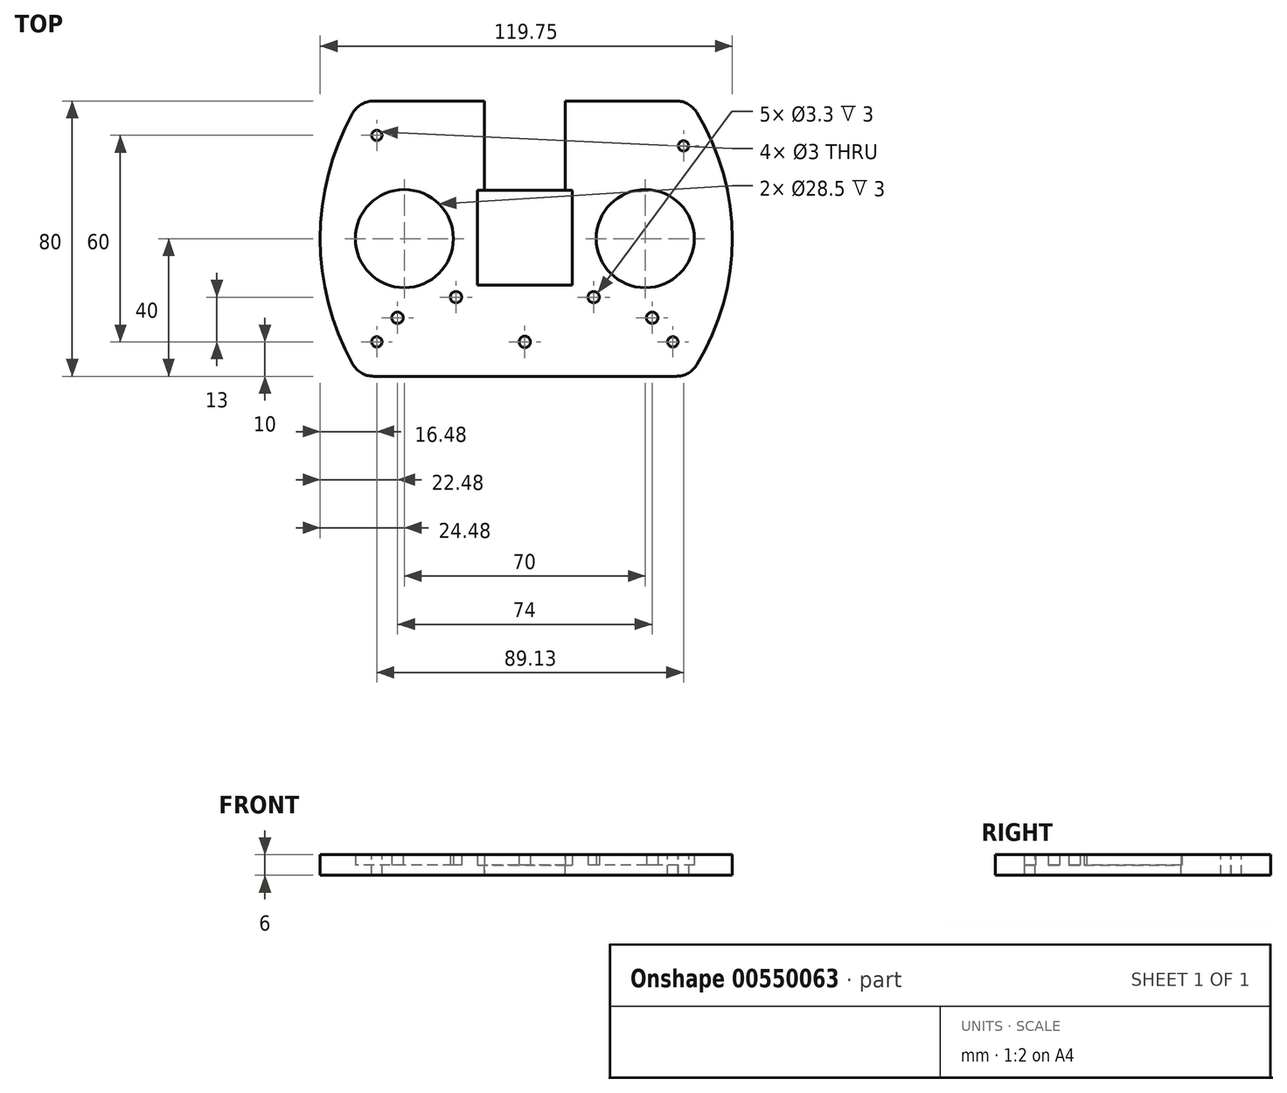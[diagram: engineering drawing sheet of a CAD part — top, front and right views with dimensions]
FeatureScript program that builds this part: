
annotation { "Feature Type Name" : "Feature", "Feature Type Description" : "" }
export const myFeature = defineFeature(function(context is Context, id is Id, definition is map)
    precondition{}
    {
        {
            var Q0;
            Q0=qCreatedBy(makeId("Top.planeOp"),FACE);
            var sketch = newSketch(context, id + "F0", { "sketchPlane" : qUnion([Q0])});
            skLineSegment(sketch, "E0.bottom", {"start": v(-45.1, 35) * mm, "end": v(45.1, 35) * mm});
            skLineSegment(sketch, "E0.top", {"start": v(-45.1, -35) * mm, "end": v(45.1, -35) * mm});
            skArc(sketch, "E1", {"start": v(-45.1, 35) * mm, "mid": v(-54.48, 0) * mm, "end": v(-45.1, -35) * mm});
            skArc(sketch, "E2", {"start": v(45.1, -35) * mm, "mid": v(55.27, 0) * mm, "end": v(45.1, 35) * mm});
            skCircle(sketch, "E3", {"center": v(-43, 30) * mm, "radius": 1.5 * mm});
            skCircle(sketch, "E4", {"center": v(-43, -30) * mm, "radius": 1.5 * mm});
            skLineSegment(sketch, "E5", {"start": v(-43, 30) * mm, "end": v(-43, -30) * mm, "construction": true});
            skCircle(sketch, "E6.MirrorC", {"center": v(43, -30) * mm, "radius": 1.5 * mm});
            skCircle(sketch, "E7.MirrorC", {"center": v(46.13, 26.95) * mm, "radius": 1.5 * mm});
            skSolve(sketch);
        }
        {
            var Q0;
            Q0=makeQuery(id+"F0.imprint","IMPRINT",FACE,{"disambiguationData":[TD([[makeQuery(id+"F0.imprint","IMPRINT",EDGE,{"derivedFrom":sQuery(id+"F0.wireOp",EDGE,"E0.bottom")}),-1.0]])]});
            extrude(context, id + "F1", {"entities" : qUnion([Q0]), "oppositeDirection" : true, "depth" : 3 * mm, "offsetDistance" : 25 * mm});
        }
        {
            var Q0;
            Q0 = qSketchRegion(id + "F0", true);
            extrude(context, id + "F2", {"entities" : qUnion([Q0]), "depth" : 3 * mm, "offsetDistance" : 25 * mm});
        }
        {
            var Q0;
            Q0=qCreatedBy(makeId("Top.planeOp"),FACE);
            var sketch = newSketch(context, id + "F3", { "sketchPlane" : qUnion([Q0])});
            skLineSegment(sketch, "E8.bottom", {"start": v(-13.75, 14) * mm, "end": v(-11.75, 14) * mm});
            skLineSegment(sketch, "E8.top", {"start": v(-13.75, -13.5) * mm, "end": v(13.75, -13.5) * mm});
            skLineSegment(sketch, "E8.left", {"start": v(-13.75, 14) * mm, "end": v(-13.75, -13.5) * mm});
            skLineSegment(sketch, "E8.right", {"start": v(13.75, 14) * mm, "end": v(13.75, -13.5) * mm});
            skCircle(sketch, "E9", {"center": v(-35, 0) * mm, "radius": 14.25 * mm});
            skCircle(sketch, "E10.MirrorC", {"center": v(35, 0) * mm, "radius": 14.25 * mm});
            skCircle(sketch, "E11", {"center": v(-37, -23) * mm, "radius": 1.65 * mm});
            skCircle(sketch, "E12", {"center": v(-20, -17) * mm, "radius": 1.65 * mm});
            skCircle(sketch, "E13", {"center": v(0, -30) * mm, "radius": 1.65 * mm});
            skCircle(sketch, "E14.MirrorC", {"center": v(37, -23) * mm, "radius": 1.65 * mm});
            skCircle(sketch, "E15.MirrorC", {"center": v(20, -17) * mm, "radius": 1.65 * mm});
            skLineSegment(sketch, "E16", {"start": v(-11.75, 14) * mm, "end": v(-11.75, 43.57) * mm});
            skLineSegment(sketch, "E17", {"start": v(-11.75, 43.57) * mm, "end": v(11.75, 43.57) * mm});
            skLineSegment(sketch, "E18", {"start": v(11.75, 43.57) * mm, "end": v(11.75, 14) * mm});
            skLineSegment(sketch, "E19.trimOffspring", {"start": v(11.75, 14) * mm, "end": v(13.75, 14) * mm});
            skSolve(sketch);
        }
        {
            var Q0;
            Q0 = qSketchRegion(id + "F3", true);
            extrude(context, id + "F4", {"entities" : qUnion([Q0]), "operationType" : NewBodyOperationType.REMOVE, "depth" : 25 * mm, "offsetDistance" : 25 * mm});
        }
        {
            var Q0;
            Q0=qCreatedBy(makeId("Top.planeOp"),FACE);
            var sketch = newSketch(context, id + "F5", { "sketchPlane" : qUnion([Q0])});
            skArc(sketch, "E20.0", {"start": v(-50.05, -36.4) * mm, "mid": v(-59.48, 0) * mm, "end": v(-50.05, 36.4) * mm});
            skLineSegment(sketch, "E20.1", {"start": v(43.99, -40) * mm, "end": v(-43.93, -40) * mm});
            skArc(sketch, "E20.2", {"start": v(49.96, 36.65) * mm, "mid": v(60.27, 0) * mm, "end": v(49.96, -36.65) * mm});
            skLineSegment(sketch, "E20.3", {"start": v(-43.93, 40) * mm, "end": v(43.99, 40) * mm});
            skArc(sketch, "E21.0", {"start": v(-44.52, -34) * mm, "mid": v(-53.48, 0) * mm, "end": v(-44.52, 34) * mm});
            skLineSegment(sketch, "E21.1", {"start": v(44.55, -34) * mm, "end": v(-44.52, -34) * mm});
            skArc(sketch, "E21.2", {"start": v(44.55, 34) * mm, "mid": v(54.27, 0) * mm, "end": v(44.55, -34) * mm});
            skLineSegment(sketch, "E21.3", {"start": v(-44.52, 34) * mm, "end": v(44.55, 34) * mm});
            skPoint(sketch, "E22.visualSharp", {"position": v(47.78, 40) * mm});
            skArc(sketch, "E22.filletArc", {"start": v(49.96, 36.65) * mm, "mid": v(47.41, 39.1) * mm, "end": v(43.99, 40) * mm});
            skPoint(sketch, "E23.visualSharp", {"position": v(47.78, -40) * mm});
            skArc(sketch, "E23.filletArc", {"start": v(43.99, -40) * mm, "mid": v(47.41, -39.1) * mm, "end": v(49.96, -36.65) * mm});
            skPoint(sketch, "E24.visualSharp", {"position": v(-47.92, -40) * mm});
            skArc(sketch, "E24.filletArc", {"start": v(-50.05, -36.4) * mm, "mid": v(-47.49, -39.03) * mm, "end": v(-43.93, -40) * mm});
            skPoint(sketch, "E25.visualSharp", {"position": v(-47.92, 40) * mm});
            skArc(sketch, "E25.filletArc", {"start": v(-43.93, 40) * mm, "mid": v(-47.49, 39.03) * mm, "end": v(-50.05, 36.4) * mm});
            skSolve(sketch);
        }
        {
            var Q0;
            Q0 = qSketchRegion(id + "F5", true);
            extrude(context, id + "F6", {"entities" : qUnion([Q0]), "operationType" : NewBodyOperationType.ADD, "oppositeDirection" : true, "depth" : 3 * mm, "offsetDistance" : 25 * mm});
        }
        {
            var Q0;
            Q0 = qSketchRegion(id + "F5", true);
            extrude(context, id + "F7", {"entities" : qUnion([Q0]), "operationType" : NewBodyOperationType.ADD, "depth" : 3 * mm, "offsetDistance" : 25 * mm});
        }
        {
            var Q0;
            Q0=makeQuery(id+"F7.boolean.opBoolean","MERGE",FACE,{"derivedFrom":[makeQuery(id+"F2.opExtrude","CAP_FACE",FACE,{"disambiguationData":[OSD([sQuery(id+"F0.wireOp",EDGE,"E0.bottom"),sQuery(id+"F0.wireOp",EDGE,"E0.top"),sQuery(id+"F0.wireOp",EDGE,"E1"),sQuery(id+"F0.wireOp",EDGE,"E2"),sQuery(id+"F0.wireOp",EDGE,"E3"),sQuery(id+"F0.wireOp",EDGE,"E4"),sQuery(id+"F0.wireOp",EDGE,"E6.MirrorC"),sQuery(id+"F0.wireOp",EDGE,"E7.MirrorC")])],"isStart":false}),makeQuery(id+"F7.opExtrude","CAP_FACE",FACE,{"disambiguationData":[OSD([sQuery(id+"F5.wireOp",EDGE,"E20.0"),sQuery(id+"F5.wireOp",EDGE,"E20.1"),sQuery(id+"F5.wireOp",EDGE,"E20.2"),sQuery(id+"F5.wireOp",EDGE,"E20.3"),sQuery(id+"F5.wireOp",EDGE,"E21.0"),sQuery(id+"F5.wireOp",EDGE,"E21.1"),sQuery(id+"F5.wireOp",EDGE,"E21.2"),sQuery(id+"F5.wireOp",EDGE,"E21.3"),sQuery(id+"F5.wireOp",EDGE,"E22.filletArc"),sQuery(id+"F5.wireOp",EDGE,"E23.filletArc"),sQuery(id+"F5.wireOp",EDGE,"E24.filletArc"),sQuery(id+"F5.wireOp",EDGE,"E25.filletArc")])],"isStart":false})]});
            var sketch = newSketch(context, id + "F8", { "sketchPlane" : qUnion([Q0])});
            skPoint(sketch, "E26.oppositeSnap0", {"position": v(-11.75, 24) * mm});
            skLineSegment(sketch, "E26.bottom", {"start": v(11.75, 14) * mm, "end": v(-11.75, 14) * mm});
            skLineSegment(sketch, "E26.top", {"start": v(11.75, 51.7) * mm, "end": v(-11.75, 51.7) * mm});
            skLineSegment(sketch, "E26.left", {"start": v(11.75, 14) * mm, "end": v(11.75, 51.7) * mm});
            skLineSegment(sketch, "E26.right", {"start": v(-11.75, 14) * mm, "end": v(-11.75, 51.7) * mm});
            skSolve(sketch);
        }
        {
            var Q0;
            Q0 = qSketchRegion(id + "F8", true);
            extrude(context, id + "F9", {"entities" : qUnion([Q0]), "operationType" : NewBodyOperationType.REMOVE, "oppositeDirection" : true, "depth" : 25 * mm, "offsetDistance" : 25 * mm});
        }
    });
